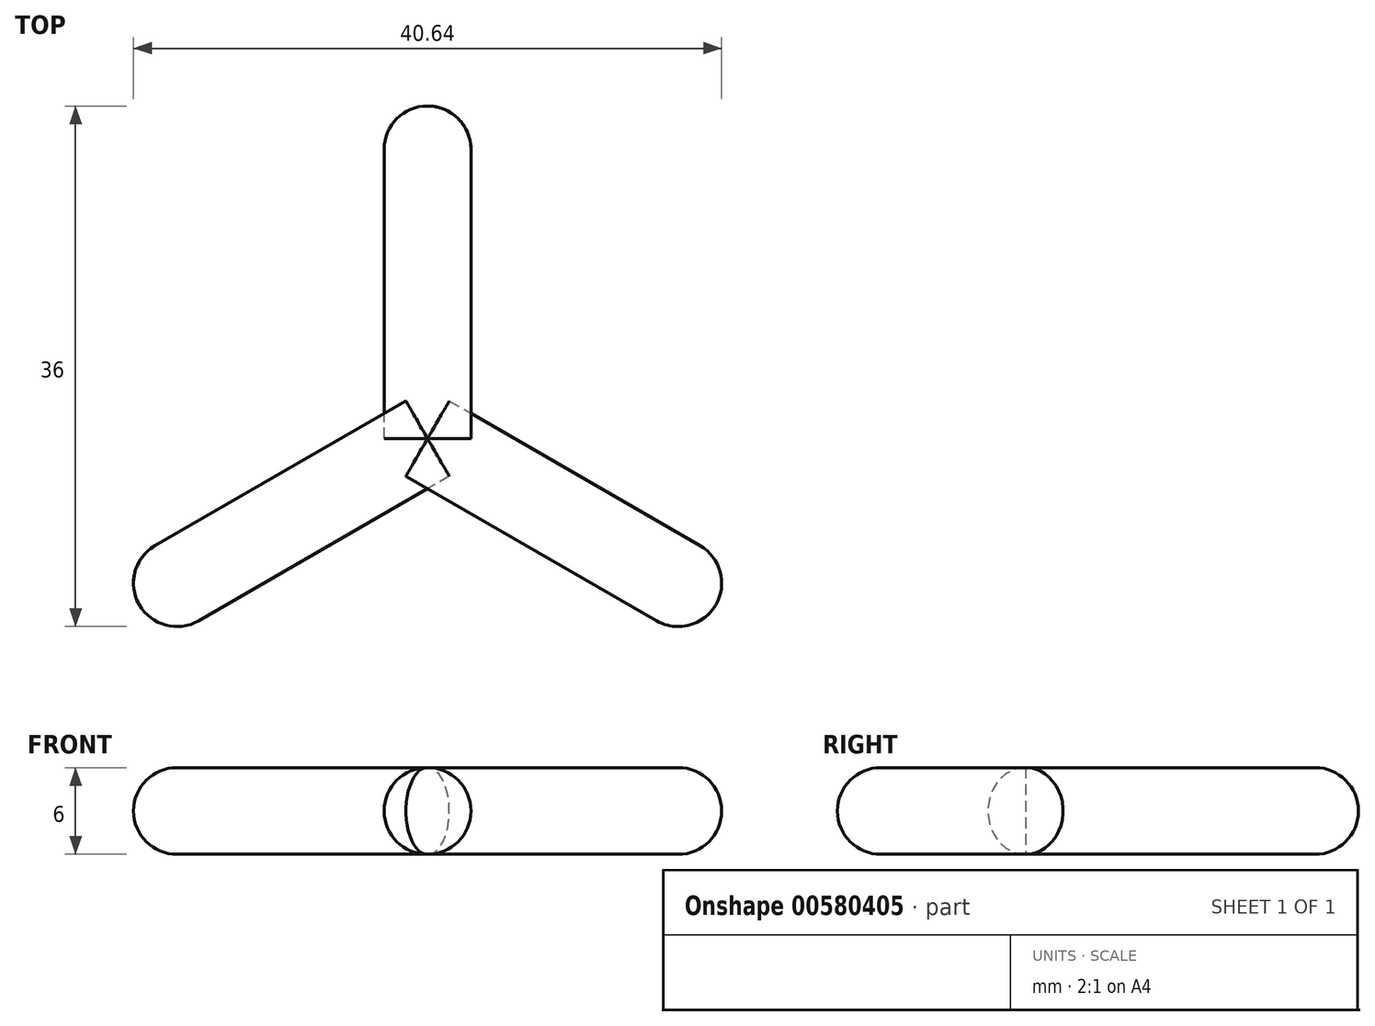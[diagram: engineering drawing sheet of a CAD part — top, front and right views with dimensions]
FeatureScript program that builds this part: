
annotation { "Feature Type Name" : "Feature", "Feature Type Description" : "" }
export const myFeature = defineFeature(function(context is Context, id is Id, definition is map)
    precondition{}
    {
        {
            var Q0;
            Q0=qCreatedBy(makeId("Top.planeOp"),FACE);
            var sketch = newSketch(context, id + "F0", { "sketchPlane" : qUnion([Q0])});
            skPoint(sketch, "E0", {"position": v(3, 0) * mm});
            skLineSegment(sketch, "E1", {"start": v(3, 0) * mm, "end": v(3, 20) * mm});
            skLineSegment(sketch, "E2", {"start": v(0, 0) * mm, "end": v(0, 23) * mm, "construction": true});
            skArc(sketch, "E3", {"start": v(0, 23) * mm, "mid": v(3, 20) * mm, "end": v(0, 17) * mm});
            skLineSegment(sketch, "E4", {"start": v(0, 23) * mm, "end": v(0, 0) * mm});
            skLineSegment(sketch, "E5", {"start": v(0, 0) * mm, "end": v(3, 0) * mm});
            skSolve(sketch);
        }
        {
            var Q0;
            Q0 = qSketchRegion(id + "F0", true);
            var Q1;
            Q1=sQuery(id+"F0.wireOp",EDGE,"E4");
            revolve(context, id + "F1", {"entities" : qUnion([Q0]), "axis" : qUnion([Q1]), "revolveType" : RevolveType.FULL});
        }
        {
            var Q0;
            Q0=qCreatedBy(makeId("Right.planeOp"),FACE);
            var sketch = newSketch(context, id + "F2", { "sketchPlane" : qUnion([Q0])});
            skLineSegment(sketch, "E6", {"start": v(0, 0) * mm, "end": v(0, -46.54) * mm, "construction": true});
            skSolve(sketch);
        }
        {
            var Q0;
            Q0=makeQuery(id+"F1.opRevolve","SWEPT_BODY",BODY,{"disambiguationData":[OSD([sQuery(id+"F0.wireOp",EDGE,"E1"),sQuery(id+"F0.wireOp",EDGE,"E3"),sQuery(id+"F0.wireOp",EDGE,"E4"),sQuery(id+"F0.wireOp",EDGE,"E5")])]});
            var Q1;
            Q1=sQuery(id+"F2.wireOp",EDGE,"E6");
            circularPattern(context, id + "F3", {"entities" : qUnion([Q0]), "axis" : qUnion([Q1]), "angle" : 360 * degree, "instanceCount" : 3, "equalSpace" : true});
        }
    });
